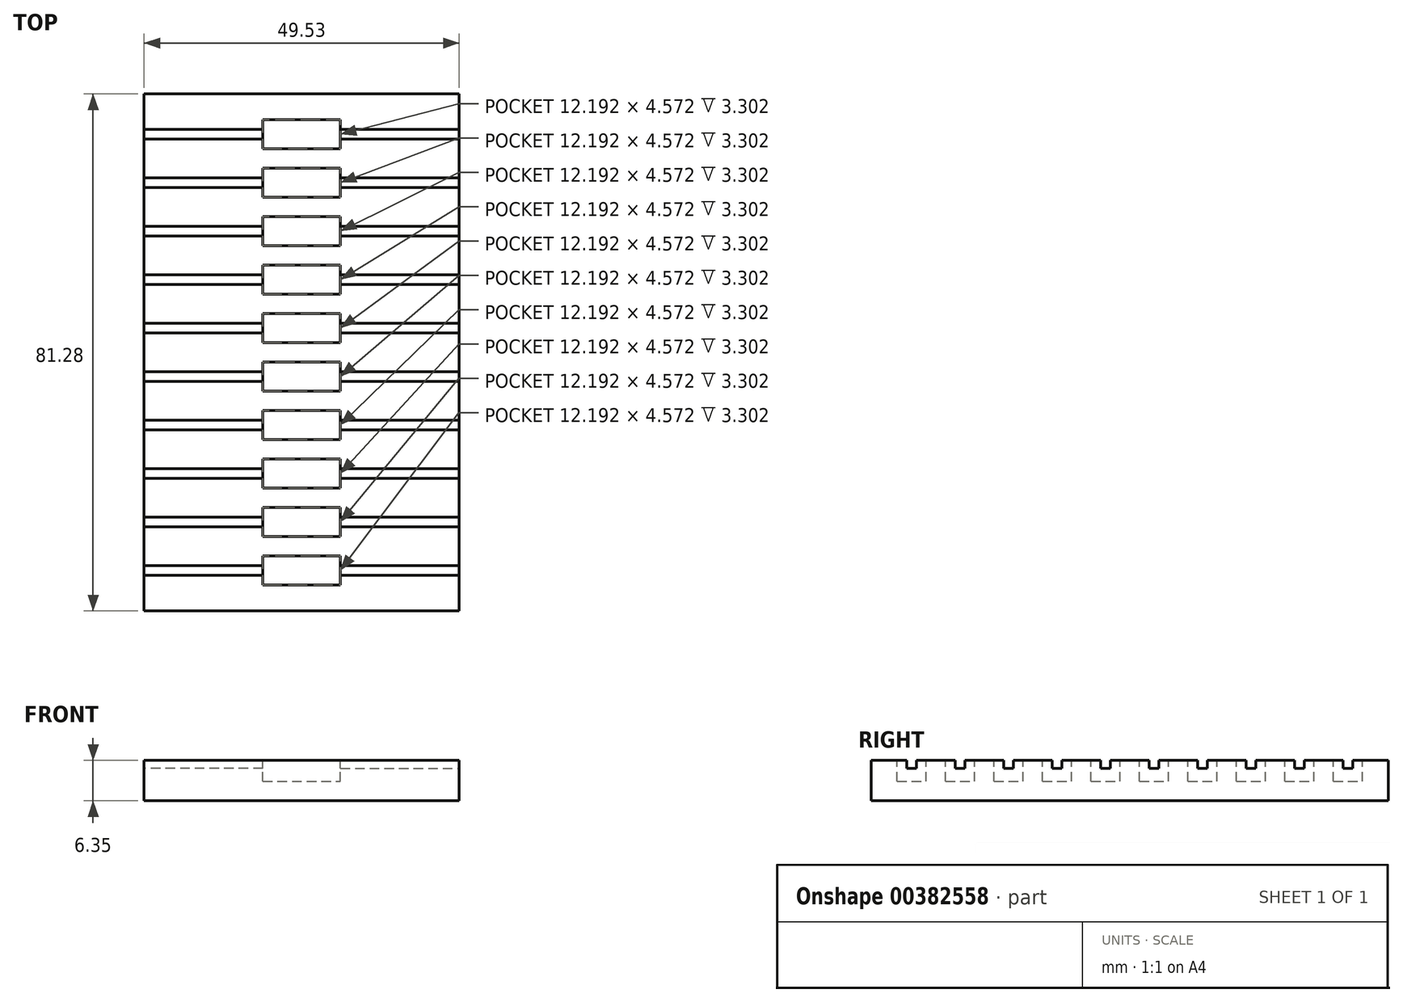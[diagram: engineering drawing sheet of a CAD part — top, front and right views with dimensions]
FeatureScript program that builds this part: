
annotation { "Feature Type Name" : "Feature", "Feature Type Description" : "" }
export const myFeature = defineFeature(function(context is Context, id is Id, definition is map)
    precondition{}
    {
        {
            var Q0;
            Q0=qCreatedBy(makeId("Top.planeOp"),FACE);
            var sketch = newSketch(context, id + "F0", { "sketchPlane" : qUnion([Q0])});
            skLineSegment(sketch, "E0.bottom", {"start": v(0, 0) * mm, "end": v(49.53, 0) * mm});
            skLineSegment(sketch, "E0.top", {"start": v(0, 81.28) * mm, "end": v(49.53, 81.28) * mm});
            skLineSegment(sketch, "E0.left", {"start": v(0, 0) * mm, "end": v(0, 81.28) * mm});
            skLineSegment(sketch, "E0.right", {"start": v(49.53, 0) * mm, "end": v(49.53, 81.28) * mm});
            skSolve(sketch);
        }
        {
            var Q0;
            Q0 = qSketchRegion(id + "F0", true);
            extrude(context, id + "F1", {"entities" : qUnion([Q0]), "depth" : 6.35 * mm});
        }
        {
            var Q0;
            Q0=makeQuery(id+"F1.opExtrude","CAP_FACE",FACE,{"disambiguationData":[OSD([sQuery(id+"F0.wireOp",EDGE,"E0.bottom"),sQuery(id+"F0.wireOp",EDGE,"E0.top"),sQuery(id+"F0.wireOp",EDGE,"E0.left"),sQuery(id+"F0.wireOp",EDGE,"E0.right")])],"isStart":false});
            var sketch = newSketch(context, id + "F2", { "sketchPlane" : qUnion([Q0])});
            skLineSegment(sketch, "E1.bottom", {"start": v(18.67, 4.06) * mm, "end": v(30.86, 4.06) * mm});
            skLineSegment(sketch, "E1.top", {"start": v(18.67, 8.64) * mm, "end": v(30.86, 8.64) * mm});
            skLineSegment(sketch, "E1.left", {"start": v(18.67, 4.06) * mm, "end": v(18.67, 8.64) * mm});
            skLineSegment(sketch, "E1.right", {"start": v(30.86, 4.06) * mm, "end": v(30.86, 8.64) * mm});
            skLineSegment(sketch, "E2", {"start": v(30.86, 6.35) * mm, "end": v(49.53, 6.35) * mm, "construction": true});
            skLineSegment(sketch, "E3.0.1.0", {"start": v(18.67, 16.26) * mm, "end": v(30.86, 16.26) * mm});
            skLineSegment(sketch, "E3.0.1.1", {"start": v(18.67, 11.68) * mm, "end": v(30.86, 11.68) * mm});
            skLineSegment(sketch, "E3.0.1.2", {"start": v(30.86, 11.68) * mm, "end": v(30.86, 16.26) * mm});
            skLineSegment(sketch, "E3.0.1.3", {"start": v(18.67, 11.68) * mm, "end": v(18.67, 16.26) * mm});
            skLineSegment(sketch, "E3.0.2.0", {"start": v(18.67, 23.88) * mm, "end": v(30.86, 23.88) * mm});
            skLineSegment(sketch, "E3.0.2.1", {"start": v(18.67, 19.3) * mm, "end": v(30.86, 19.3) * mm});
            skLineSegment(sketch, "E3.0.2.2", {"start": v(30.86, 19.3) * mm, "end": v(30.86, 23.88) * mm});
            skLineSegment(sketch, "E3.0.2.3", {"start": v(18.67, 19.3) * mm, "end": v(18.67, 23.88) * mm});
            skLineSegment(sketch, "E3.0.3.0", {"start": v(18.67, 31.5) * mm, "end": v(30.86, 31.5) * mm});
            skLineSegment(sketch, "E3.0.3.1", {"start": v(18.67, 26.92) * mm, "end": v(30.86, 26.92) * mm});
            skLineSegment(sketch, "E3.0.3.2", {"start": v(30.86, 26.92) * mm, "end": v(30.86, 31.5) * mm});
            skLineSegment(sketch, "E3.0.3.3", {"start": v(18.67, 26.92) * mm, "end": v(18.67, 31.5) * mm});
            skLineSegment(sketch, "E3.0.4.0", {"start": v(18.67, 39.12) * mm, "end": v(30.86, 39.12) * mm});
            skLineSegment(sketch, "E3.0.4.1", {"start": v(18.67, 34.54) * mm, "end": v(30.86, 34.54) * mm});
            skLineSegment(sketch, "E3.0.4.2", {"start": v(30.86, 34.54) * mm, "end": v(30.86, 39.12) * mm});
            skLineSegment(sketch, "E3.0.4.3", {"start": v(18.67, 34.54) * mm, "end": v(18.67, 39.12) * mm});
            skLineSegment(sketch, "E3.0.5.0", {"start": v(18.67, 46.74) * mm, "end": v(30.86, 46.74) * mm});
            skLineSegment(sketch, "E3.0.5.1", {"start": v(18.67, 42.16) * mm, "end": v(30.86, 42.16) * mm});
            skLineSegment(sketch, "E3.0.5.2", {"start": v(30.86, 42.16) * mm, "end": v(30.86, 46.74) * mm});
            skLineSegment(sketch, "E3.0.5.3", {"start": v(18.67, 42.16) * mm, "end": v(18.67, 46.74) * mm});
            skLineSegment(sketch, "E3.0.6.0", {"start": v(18.67, 54.36) * mm, "end": v(30.86, 54.36) * mm});
            skLineSegment(sketch, "E3.0.6.1", {"start": v(18.67, 49.78) * mm, "end": v(30.86, 49.78) * mm});
            skLineSegment(sketch, "E3.0.6.2", {"start": v(30.86, 49.78) * mm, "end": v(30.86, 54.36) * mm});
            skLineSegment(sketch, "E3.0.6.3", {"start": v(18.67, 49.78) * mm, "end": v(18.67, 54.36) * mm});
            skLineSegment(sketch, "E3.0.7.0", {"start": v(18.67, 61.98) * mm, "end": v(30.86, 61.98) * mm});
            skLineSegment(sketch, "E3.0.7.1", {"start": v(18.67, 57.4) * mm, "end": v(30.86, 57.4) * mm});
            skLineSegment(sketch, "E3.0.7.2", {"start": v(30.86, 57.4) * mm, "end": v(30.86, 61.98) * mm});
            skLineSegment(sketch, "E3.0.7.3", {"start": v(18.67, 57.4) * mm, "end": v(18.67, 61.98) * mm});
            skLineSegment(sketch, "E3.0.8.0", {"start": v(18.67, 69.6) * mm, "end": v(30.86, 69.6) * mm});
            skLineSegment(sketch, "E3.0.8.1", {"start": v(18.67, 65.02) * mm, "end": v(30.86, 65.02) * mm});
            skLineSegment(sketch, "E3.0.8.2", {"start": v(30.86, 65.02) * mm, "end": v(30.86, 69.6) * mm});
            skLineSegment(sketch, "E3.0.8.3", {"start": v(18.67, 65.02) * mm, "end": v(18.67, 69.6) * mm});
            skLineSegment(sketch, "E3.0.9.0", {"start": v(18.67, 77.22) * mm, "end": v(30.86, 77.22) * mm});
            skLineSegment(sketch, "E3.0.9.1", {"start": v(18.67, 72.64) * mm, "end": v(30.86, 72.64) * mm});
            skLineSegment(sketch, "E3.0.9.2", {"start": v(30.86, 72.64) * mm, "end": v(30.86, 77.22) * mm});
            skLineSegment(sketch, "E3.0.9.3", {"start": v(18.67, 72.64) * mm, "end": v(18.67, 77.22) * mm});
            skLineSegment(sketch, "E3.direction1", {"start": v(18.67, 4.06) * mm, "end": v(44.2, 4.06) * mm, "construction": true});
            skLineSegment(sketch, "E3.direction2", {"start": v(18.67, 4.06) * mm, "end": v(18.67, 11.68) * mm, "construction": true});
            skSolve(sketch);
        }
        {
            var Q0;
            Q0 = qSketchRegion(id + "F2", true);
            extrude(context, id + "F3", {"entities" : qUnion([Q0]), "operationType" : NewBodyOperationType.REMOVE, "oppositeDirection" : true, "depth" : 3.3 * mm});
        }
        {
            var Q0;
            Q0=makeQuery(id+"F1.opExtrude","CAP_FACE",FACE,{"disambiguationData":[OSD([sQuery(id+"F0.wireOp",EDGE,"E0.bottom"),sQuery(id+"F0.wireOp",EDGE,"E0.top"),sQuery(id+"F0.wireOp",EDGE,"E0.left"),sQuery(id+"F0.wireOp",EDGE,"E0.right")])],"isStart":false});
            var sketch = newSketch(context, id + "F4", { "sketchPlane" : qUnion([Q0])});
            skLineSegment(sketch, "E4.bottom", {"start": v(30.86, 5.59) * mm, "end": v(49.53, 5.59) * mm});
            skLineSegment(sketch, "E4.top", {"start": v(30.86, 7.11) * mm, "end": v(49.53, 7.11) * mm});
            skLineSegment(sketch, "E4.left", {"start": v(30.86, 5.59) * mm, "end": v(30.86, 7.11) * mm});
            skLineSegment(sketch, "E4.right", {"start": v(49.53, 5.59) * mm, "end": v(49.53, 7.11) * mm});
            skPoint(sketch, "E5.firstSnap0", {"position": v(40.2, 7.11) * mm});
            skLineSegment(sketch, "E5.bottom", {"start": v(18.67, 7.11) * mm, "end": v(0, 7.11) * mm});
            skLineSegment(sketch, "E5.top", {"start": v(18.67, 5.59) * mm, "end": v(0, 5.59) * mm});
            skLineSegment(sketch, "E5.left", {"start": v(18.67, 7.11) * mm, "end": v(18.67, 5.59) * mm});
            skLineSegment(sketch, "E5.right", {"start": v(0, 7.11) * mm, "end": v(0, 5.59) * mm});
            skLineSegment(sketch, "E6", {"start": v(30.86, 6.35) * mm, "end": v(49.53, 6.35) * mm, "construction": true});
            skLineSegment(sketch, "E7.0.1.0", {"start": v(18.67, 13.2) * mm, "end": v(0, 13.2) * mm});
            skLineSegment(sketch, "E7.0.1.1", {"start": v(30.86, 13.97) * mm, "end": v(49.53, 13.97) * mm, "construction": true});
            skLineSegment(sketch, "E7.0.1.2", {"start": v(18.67, 14.73) * mm, "end": v(0, 14.73) * mm});
            skLineSegment(sketch, "E7.0.1.3", {"start": v(30.86, 14.73) * mm, "end": v(49.53, 14.73) * mm});
            skLineSegment(sketch, "E7.0.1.4", {"start": v(30.86, 13.2) * mm, "end": v(49.53, 13.2) * mm});
            skPoint(sketch, "E7.0.1.5", {"position": v(40.2, 14.73) * mm});
            skLineSegment(sketch, "E7.0.1.6", {"start": v(18.67, 14.73) * mm, "end": v(18.67, 13.2) * mm});
            skLineSegment(sketch, "E7.0.1.7", {"start": v(0, 14.73) * mm, "end": v(0, 13.2) * mm});
            skLineSegment(sketch, "E7.0.1.8", {"start": v(49.53, 13.2) * mm, "end": v(49.53, 14.73) * mm});
            skLineSegment(sketch, "E7.0.1.9", {"start": v(30.86, 13.2) * mm, "end": v(30.86, 14.73) * mm});
            skLineSegment(sketch, "E7.0.2.0", {"start": v(18.67, 20.83) * mm, "end": v(0, 20.83) * mm});
            skLineSegment(sketch, "E7.0.2.1", {"start": v(30.86, 21.6) * mm, "end": v(49.53, 21.6) * mm, "construction": true});
            skLineSegment(sketch, "E7.0.2.2", {"start": v(18.67, 22.35) * mm, "end": v(0, 22.35) * mm});
            skLineSegment(sketch, "E7.0.2.3", {"start": v(30.86, 22.35) * mm, "end": v(49.53, 22.35) * mm});
            skLineSegment(sketch, "E7.0.2.4", {"start": v(30.86, 20.83) * mm, "end": v(49.53, 20.83) * mm});
            skPoint(sketch, "E7.0.2.5", {"position": v(40.2, 22.35) * mm});
            skLineSegment(sketch, "E7.0.2.6", {"start": v(18.67, 22.35) * mm, "end": v(18.67, 20.83) * mm});
            skLineSegment(sketch, "E7.0.2.7", {"start": v(0, 22.35) * mm, "end": v(0, 20.83) * mm});
            skLineSegment(sketch, "E7.0.2.8", {"start": v(49.53, 20.83) * mm, "end": v(49.53, 22.35) * mm});
            skLineSegment(sketch, "E7.0.2.9", {"start": v(30.86, 20.83) * mm, "end": v(30.86, 22.35) * mm});
            skLineSegment(sketch, "E7.0.3.0", {"start": v(18.67, 28.45) * mm, "end": v(0, 28.45) * mm});
            skLineSegment(sketch, "E7.0.3.1", {"start": v(30.86, 29.21) * mm, "end": v(49.53, 29.21) * mm, "construction": true});
            skLineSegment(sketch, "E7.0.3.2", {"start": v(18.67, 29.97) * mm, "end": v(0, 29.97) * mm});
            skLineSegment(sketch, "E7.0.3.3", {"start": v(30.86, 29.97) * mm, "end": v(49.53, 29.97) * mm});
            skLineSegment(sketch, "E7.0.3.4", {"start": v(30.86, 28.45) * mm, "end": v(49.53, 28.45) * mm});
            skPoint(sketch, "E7.0.3.5", {"position": v(40.2, 29.97) * mm});
            skLineSegment(sketch, "E7.0.3.6", {"start": v(18.67, 29.97) * mm, "end": v(18.67, 28.45) * mm});
            skLineSegment(sketch, "E7.0.3.7", {"start": v(0, 29.97) * mm, "end": v(0, 28.45) * mm});
            skLineSegment(sketch, "E7.0.3.8", {"start": v(49.53, 28.45) * mm, "end": v(49.53, 29.97) * mm});
            skLineSegment(sketch, "E7.0.3.9", {"start": v(30.86, 28.45) * mm, "end": v(30.86, 29.97) * mm});
            skLineSegment(sketch, "E7.0.4.0", {"start": v(18.67, 36.07) * mm, "end": v(0, 36.07) * mm});
            skLineSegment(sketch, "E7.0.4.1", {"start": v(30.86, 36.83) * mm, "end": v(49.53, 36.83) * mm, "construction": true});
            skLineSegment(sketch, "E7.0.4.2", {"start": v(18.67, 37.6) * mm, "end": v(0, 37.6) * mm});
            skLineSegment(sketch, "E7.0.4.3", {"start": v(30.86, 37.6) * mm, "end": v(49.53, 37.6) * mm});
            skLineSegment(sketch, "E7.0.4.4", {"start": v(30.86, 36.07) * mm, "end": v(49.53, 36.07) * mm});
            skPoint(sketch, "E7.0.4.5", {"position": v(40.2, 37.6) * mm});
            skLineSegment(sketch, "E7.0.4.6", {"start": v(18.67, 37.6) * mm, "end": v(18.67, 36.07) * mm});
            skLineSegment(sketch, "E7.0.4.7", {"start": v(0, 37.6) * mm, "end": v(0, 36.07) * mm});
            skLineSegment(sketch, "E7.0.4.8", {"start": v(49.53, 36.07) * mm, "end": v(49.53, 37.6) * mm});
            skLineSegment(sketch, "E7.0.4.9", {"start": v(30.86, 36.07) * mm, "end": v(30.86, 37.6) * mm});
            skLineSegment(sketch, "E7.0.5.0", {"start": v(18.67, 43.69) * mm, "end": v(0, 43.69) * mm});
            skLineSegment(sketch, "E7.0.5.1", {"start": v(30.86, 44.45) * mm, "end": v(49.53, 44.45) * mm, "construction": true});
            skLineSegment(sketch, "E7.0.5.2", {"start": v(18.67, 45.21) * mm, "end": v(0, 45.21) * mm});
            skLineSegment(sketch, "E7.0.5.3", {"start": v(30.86, 45.21) * mm, "end": v(49.53, 45.21) * mm});
            skLineSegment(sketch, "E7.0.5.4", {"start": v(30.86, 43.69) * mm, "end": v(49.53, 43.69) * mm});
            skPoint(sketch, "E7.0.5.5", {"position": v(40.2, 45.21) * mm});
            skLineSegment(sketch, "E7.0.5.6", {"start": v(18.67, 45.21) * mm, "end": v(18.67, 43.69) * mm});
            skLineSegment(sketch, "E7.0.5.7", {"start": v(0, 45.21) * mm, "end": v(0, 43.69) * mm});
            skLineSegment(sketch, "E7.0.5.8", {"start": v(49.53, 43.69) * mm, "end": v(49.53, 45.21) * mm});
            skLineSegment(sketch, "E7.0.5.9", {"start": v(30.86, 43.69) * mm, "end": v(30.86, 45.21) * mm});
            skLineSegment(sketch, "E7.0.6.0", {"start": v(18.67, 51.3) * mm, "end": v(0, 51.3) * mm});
            skLineSegment(sketch, "E7.0.6.1", {"start": v(30.86, 52.07) * mm, "end": v(49.53, 52.07) * mm, "construction": true});
            skLineSegment(sketch, "E7.0.6.2", {"start": v(18.67, 52.83) * mm, "end": v(0, 52.83) * mm});
            skLineSegment(sketch, "E7.0.6.3", {"start": v(30.86, 52.83) * mm, "end": v(49.53, 52.83) * mm});
            skLineSegment(sketch, "E7.0.6.4", {"start": v(30.86, 51.3) * mm, "end": v(49.53, 51.3) * mm});
            skPoint(sketch, "E7.0.6.5", {"position": v(40.2, 52.83) * mm});
            skLineSegment(sketch, "E7.0.6.6", {"start": v(18.67, 52.83) * mm, "end": v(18.67, 51.3) * mm});
            skLineSegment(sketch, "E7.0.6.7", {"start": v(0, 52.83) * mm, "end": v(0, 51.3) * mm});
            skLineSegment(sketch, "E7.0.6.8", {"start": v(49.53, 51.3) * mm, "end": v(49.53, 52.83) * mm});
            skLineSegment(sketch, "E7.0.6.9", {"start": v(30.86, 51.3) * mm, "end": v(30.86, 52.83) * mm});
            skLineSegment(sketch, "E7.0.7.0", {"start": v(18.67, 58.93) * mm, "end": v(0, 58.93) * mm});
            skLineSegment(sketch, "E7.0.7.1", {"start": v(30.86, 59.69) * mm, "end": v(49.53, 59.69) * mm, "construction": true});
            skLineSegment(sketch, "E7.0.7.2", {"start": v(18.67, 60.45) * mm, "end": v(0, 60.45) * mm});
            skLineSegment(sketch, "E7.0.7.3", {"start": v(30.86, 60.45) * mm, "end": v(49.53, 60.45) * mm});
            skLineSegment(sketch, "E7.0.7.4", {"start": v(30.86, 58.93) * mm, "end": v(49.53, 58.93) * mm});
            skPoint(sketch, "E7.0.7.5", {"position": v(40.2, 60.45) * mm});
            skLineSegment(sketch, "E7.0.7.6", {"start": v(18.67, 60.45) * mm, "end": v(18.67, 58.93) * mm});
            skLineSegment(sketch, "E7.0.7.7", {"start": v(0, 60.45) * mm, "end": v(0, 58.93) * mm});
            skLineSegment(sketch, "E7.0.7.8", {"start": v(49.53, 58.93) * mm, "end": v(49.53, 60.45) * mm});
            skLineSegment(sketch, "E7.0.7.9", {"start": v(30.86, 58.93) * mm, "end": v(30.86, 60.45) * mm});
            skLineSegment(sketch, "E7.0.8.0", {"start": v(18.67, 66.55) * mm, "end": v(0, 66.55) * mm});
            skLineSegment(sketch, "E7.0.8.1", {"start": v(30.86, 67.3) * mm, "end": v(49.53, 67.3) * mm, "construction": true});
            skLineSegment(sketch, "E7.0.8.2", {"start": v(18.67, 68.07) * mm, "end": v(0, 68.07) * mm});
            skLineSegment(sketch, "E7.0.8.3", {"start": v(30.86, 68.07) * mm, "end": v(49.53, 68.07) * mm});
            skLineSegment(sketch, "E7.0.8.4", {"start": v(30.86, 66.55) * mm, "end": v(49.53, 66.55) * mm});
            skPoint(sketch, "E7.0.8.5", {"position": v(40.2, 68.07) * mm});
            skLineSegment(sketch, "E7.0.8.6", {"start": v(18.67, 68.07) * mm, "end": v(18.67, 66.55) * mm});
            skLineSegment(sketch, "E7.0.8.7", {"start": v(0, 68.07) * mm, "end": v(0, 66.55) * mm});
            skLineSegment(sketch, "E7.0.8.8", {"start": v(49.53, 66.55) * mm, "end": v(49.53, 68.07) * mm});
            skLineSegment(sketch, "E7.0.8.9", {"start": v(30.86, 66.55) * mm, "end": v(30.86, 68.07) * mm});
            skLineSegment(sketch, "E7.0.9.0", {"start": v(18.67, 74.17) * mm, "end": v(0, 74.17) * mm});
            skLineSegment(sketch, "E7.0.9.1", {"start": v(30.86, 74.93) * mm, "end": v(49.53, 74.93) * mm, "construction": true});
            skLineSegment(sketch, "E7.0.9.2", {"start": v(18.67, 75.7) * mm, "end": v(0, 75.7) * mm});
            skLineSegment(sketch, "E7.0.9.3", {"start": v(30.86, 75.7) * mm, "end": v(49.53, 75.7) * mm});
            skLineSegment(sketch, "E7.0.9.4", {"start": v(30.86, 74.17) * mm, "end": v(49.53, 74.17) * mm});
            skPoint(sketch, "E7.0.9.5", {"position": v(40.2, 75.7) * mm});
            skLineSegment(sketch, "E7.0.9.6", {"start": v(18.67, 75.7) * mm, "end": v(18.67, 74.17) * mm});
            skLineSegment(sketch, "E7.0.9.7", {"start": v(0, 75.7) * mm, "end": v(0, 74.17) * mm});
            skLineSegment(sketch, "E7.0.9.8", {"start": v(49.53, 74.17) * mm, "end": v(49.53, 75.7) * mm});
            skLineSegment(sketch, "E7.0.9.9", {"start": v(30.86, 74.17) * mm, "end": v(30.86, 75.7) * mm});
            skLineSegment(sketch, "E7.direction1", {"start": v(0, 5.59) * mm, "end": v(25.4, 5.59) * mm, "construction": true});
            skLineSegment(sketch, "E7.direction2", {"start": v(0, 5.59) * mm, "end": v(0, 13.2) * mm, "construction": true});
            skSolve(sketch);
        }
        {
            var Q0;
            Q0 = qSketchRegion(id + "F4", true);
            extrude(context, id + "F5", {"entities" : qUnion([Q0]), "operationType" : NewBodyOperationType.REMOVE, "oppositeDirection" : true, "depth" : 1.27 * mm});
        }
    });
